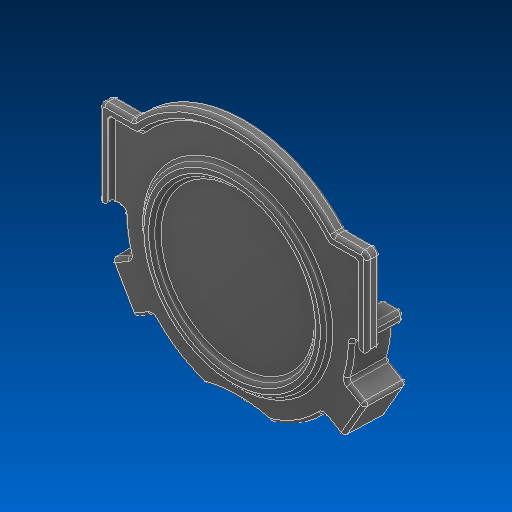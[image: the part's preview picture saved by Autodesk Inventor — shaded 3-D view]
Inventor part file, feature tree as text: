
AUTODESK INVENTOR PART (.ipt)
format: ipt  version: 2022.2 (Build 262287000, 287)  size: 783,360 bytes
history: native  units: in
note: dims shown in document units (in); Inventor stores cm internally (conversion verified against a paired STEP export)
features: fillet x1
ambient origin geometry x8: Origin, YZ Plane, XZ Plane, XY Plane, X Axis, Y Axis, Z Axis, Center Point
bodies: Solid1 (feature_tree)
feature tree (1):
  fillet  "Fillet13"  [1 undecoded]
note: 1 required parameter value undecoded (feature->parameter linkage not recoverable at this tier; creation-order binding heuristic only, values carry confidence <= 0.55)
